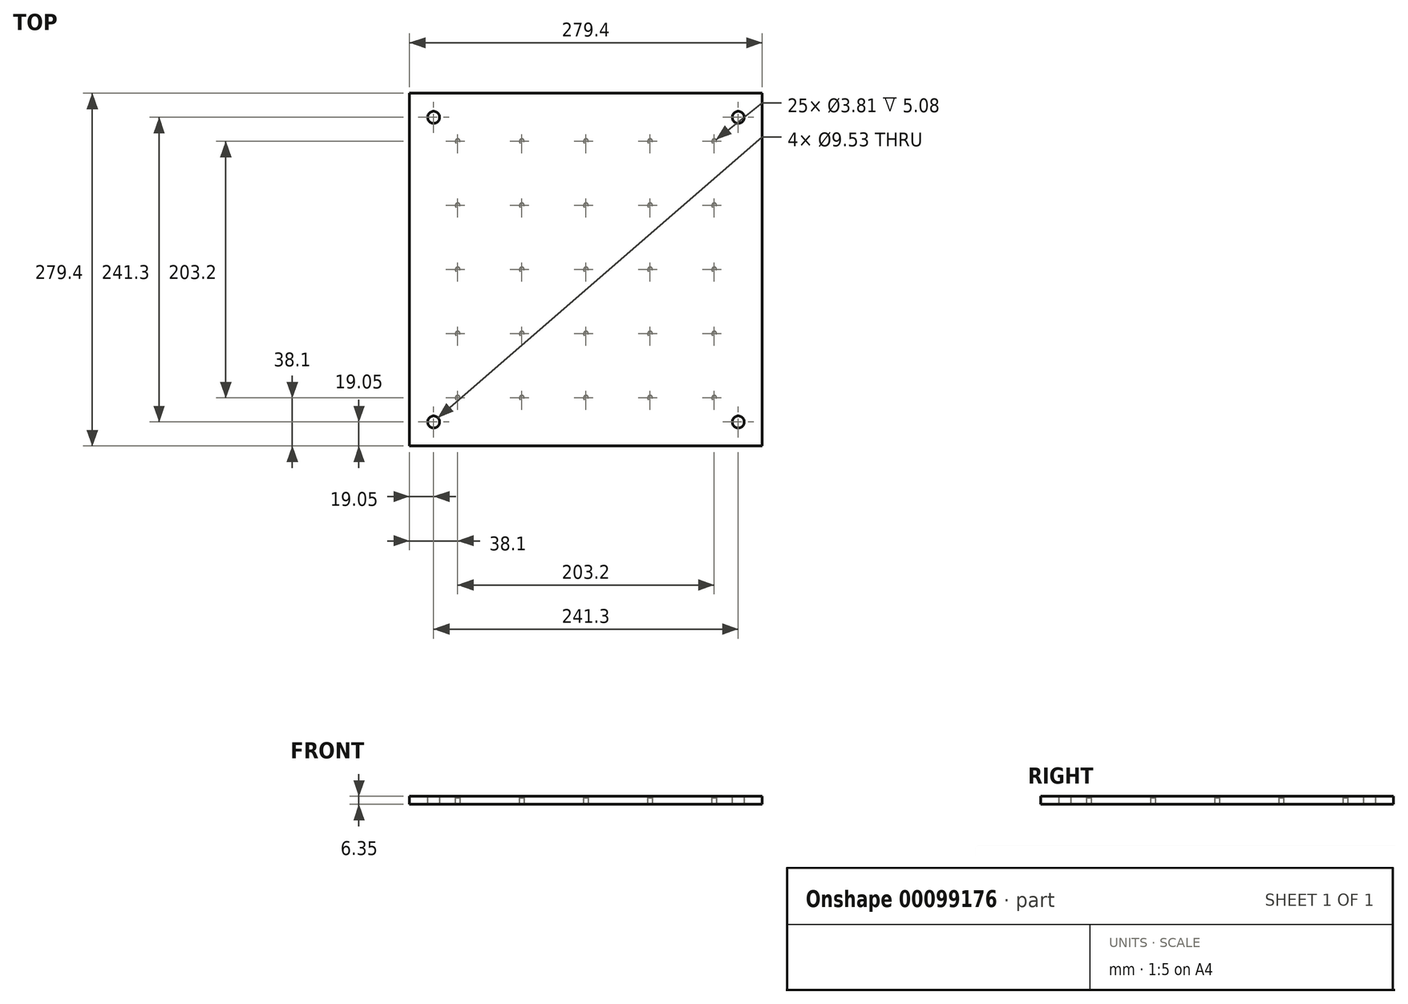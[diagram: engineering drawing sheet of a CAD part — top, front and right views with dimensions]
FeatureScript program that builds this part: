
annotation { "Feature Type Name" : "Feature", "Feature Type Description" : "" }
export const myFeature = defineFeature(function(context is Context, id is Id, definition is map)
    precondition{}
    {
        {
            var Q0;
            Q0=qCreatedBy(makeId("Top.planeOp"),FACE);
            var sketch = newSketch(context, id + "F0", { "sketchPlane" : qUnion([Q0])});
            skLineSegment(sketch, "E0.bottom", {"start": v(0, 0) * mm, "end": v(279.4, 0) * mm});
            skLineSegment(sketch, "E0.top", {"start": v(0, 279.4) * mm, "end": v(279.4, 279.4) * mm});
            skLineSegment(sketch, "E0.left", {"start": v(0, 0) * mm, "end": v(0, 279.4) * mm});
            skLineSegment(sketch, "E0.right", {"start": v(279.4, 0) * mm, "end": v(279.4, 279.4) * mm});
            skSolve(sketch);
        }
        {
            var Q0;
            Q0=makeQuery(id+"F0.imprint","IMPRINT",FACE,{"disambiguationData":[TD([[makeQuery(id+"F0.imprint","IMPRINT",EDGE,{"derivedFrom":sQuery(id+"F0.wireOp",EDGE,"E0.bottom")}),1.0]])]});
            extrude(context, id + "F1", {"entities" : qUnion([Q0]), "depth" : 6.35 * mm});
        }
        {
            var Q0;
            Q0=makeQuery(id+"F1.opExtrude","CAP_FACE",FACE,{"disambiguationData":[OSD([sQuery(id+"F0.wireOp",EDGE,"E0.bottom"),sQuery(id+"F0.wireOp",EDGE,"E0.top"),sQuery(id+"F0.wireOp",EDGE,"E0.left"),sQuery(id+"F0.wireOp",EDGE,"E0.right")])],"isStart":true});
            var sketch = newSketch(context, id + "F2", { "sketchPlane" : qUnion([Q0])});
            skLineSegment(sketch, "E1", {"start": v(0, 0) * mm, "end": v(38.1, 0) * mm, "construction": true});
            skLineSegment(sketch, "E2", {"start": v(38.1, 0) * mm, "end": v(38.1, -38.1) * mm, "construction": true});
            skCircle(sketch, "E3", {"center": v(38.1, -38.1) * mm, "radius": 22.23 * mm, "construction": true});
            skCircle(sketch, "E4.1.0.0", {"center": v(88.9, -38.1) * mm, "radius": 22.23 * mm, "construction": true});
            skCircle(sketch, "E4.2.0.0", {"center": v(139.7, -38.1) * mm, "radius": 22.23 * mm, "construction": true});
            skCircle(sketch, "E4.3.0.0", {"center": v(190.5, -38.1) * mm, "radius": 22.23 * mm, "construction": true});
            skCircle(sketch, "E4.4.0.0", {"center": v(241.3, -38.1) * mm, "radius": 22.23 * mm, "construction": true});
            skLineSegment(sketch, "E4.direction1", {"start": v(38.1, -38.1) * mm, "end": v(88.9, -38.1) * mm, "construction": true});
            skCircle(sketch, "E5.1.0.0", {"center": v(38.1, -88.9) * mm, "radius": 22.23 * mm, "construction": true});
            skCircle(sketch, "E5.1.0.1", {"center": v(88.9, -88.9) * mm, "radius": 22.23 * mm, "construction": true});
            skCircle(sketch, "E5.1.0.2", {"center": v(139.7, -88.9) * mm, "radius": 22.23 * mm, "construction": true});
            skCircle(sketch, "E5.1.0.3", {"center": v(190.5, -88.9) * mm, "radius": 22.23 * mm, "construction": true});
            skCircle(sketch, "E5.1.0.4", {"center": v(241.3, -88.9) * mm, "radius": 22.23 * mm, "construction": true});
            skCircle(sketch, "E5.2.0.0", {"center": v(38.1, -139.7) * mm, "radius": 22.23 * mm, "construction": true});
            skCircle(sketch, "E5.2.0.1", {"center": v(88.9, -139.7) * mm, "radius": 22.23 * mm, "construction": true});
            skCircle(sketch, "E5.2.0.2", {"center": v(139.7, -139.7) * mm, "radius": 22.23 * mm, "construction": true});
            skCircle(sketch, "E5.2.0.3", {"center": v(190.5, -139.7) * mm, "radius": 22.23 * mm, "construction": true});
            skCircle(sketch, "E5.2.0.4", {"center": v(241.3, -139.7) * mm, "radius": 22.23 * mm, "construction": true});
            skCircle(sketch, "E5.3.0.0", {"center": v(38.1, -190.5) * mm, "radius": 22.23 * mm, "construction": true});
            skCircle(sketch, "E5.3.0.1", {"center": v(88.9, -190.5) * mm, "radius": 22.23 * mm, "construction": true});
            skCircle(sketch, "E5.3.0.2", {"center": v(139.7, -190.5) * mm, "radius": 22.23 * mm, "construction": true});
            skCircle(sketch, "E5.3.0.3", {"center": v(190.5, -190.5) * mm, "radius": 22.23 * mm, "construction": true});
            skCircle(sketch, "E5.3.0.4", {"center": v(241.3, -190.5) * mm, "radius": 22.23 * mm, "construction": true});
            skCircle(sketch, "E5.4.0.0", {"center": v(38.1, -241.3) * mm, "radius": 22.23 * mm, "construction": true});
            skCircle(sketch, "E5.4.0.1", {"center": v(88.9, -241.3) * mm, "radius": 22.23 * mm, "construction": true});
            skCircle(sketch, "E5.4.0.2", {"center": v(139.7, -241.3) * mm, "radius": 22.23 * mm, "construction": true});
            skCircle(sketch, "E5.4.0.3", {"center": v(190.5, -241.3) * mm, "radius": 22.23 * mm, "construction": true});
            skCircle(sketch, "E5.4.0.4", {"center": v(241.3, -241.3) * mm, "radius": 22.23 * mm, "construction": true});
            skLineSegment(sketch, "E5.direction1", {"start": v(38.1, -38.1) * mm, "end": v(38.1, -88.9) * mm, "construction": true});
            skCircle(sketch, "E6", {"center": v(38.1, -38.1) * mm, "radius": 1.9 * mm});
            skCircle(sketch, "E7.0.1.0", {"center": v(38.1, -88.9) * mm, "radius": 1.9 * mm});
            skCircle(sketch, "E7.0.2.0", {"center": v(38.1, -139.7) * mm, "radius": 1.9 * mm});
            skCircle(sketch, "E7.0.3.0", {"center": v(38.1, -190.5) * mm, "radius": 1.9 * mm});
            skCircle(sketch, "E7.0.4.0", {"center": v(38.1, -241.3) * mm, "radius": 1.9 * mm});
            skCircle(sketch, "E7.1.0.0", {"center": v(88.9, -38.1) * mm, "radius": 1.9 * mm});
            skCircle(sketch, "E7.1.1.0", {"center": v(88.9, -88.9) * mm, "radius": 1.9 * mm});
            skCircle(sketch, "E7.1.2.0", {"center": v(88.9, -139.7) * mm, "radius": 1.9 * mm});
            skCircle(sketch, "E7.1.3.0", {"center": v(88.9, -190.5) * mm, "radius": 1.9 * mm});
            skCircle(sketch, "E7.1.4.0", {"center": v(88.9, -241.3) * mm, "radius": 1.9 * mm});
            skCircle(sketch, "E7.2.0.0", {"center": v(139.7, -38.1) * mm, "radius": 1.9 * mm});
            skCircle(sketch, "E7.2.1.0", {"center": v(139.7, -88.9) * mm, "radius": 1.9 * mm});
            skCircle(sketch, "E7.2.2.0", {"center": v(139.7, -139.7) * mm, "radius": 1.9 * mm});
            skCircle(sketch, "E7.2.3.0", {"center": v(139.7, -190.5) * mm, "radius": 1.9 * mm});
            skCircle(sketch, "E7.2.4.0", {"center": v(139.7, -241.3) * mm, "radius": 1.9 * mm});
            skCircle(sketch, "E7.3.0.0", {"center": v(190.5, -38.1) * mm, "radius": 1.9 * mm});
            skCircle(sketch, "E7.3.1.0", {"center": v(190.5, -88.9) * mm, "radius": 1.9 * mm});
            skCircle(sketch, "E7.3.2.0", {"center": v(190.5, -139.7) * mm, "radius": 1.9 * mm});
            skCircle(sketch, "E7.3.3.0", {"center": v(190.5, -190.5) * mm, "radius": 1.9 * mm});
            skCircle(sketch, "E7.3.4.0", {"center": v(190.5, -241.3) * mm, "radius": 1.9 * mm});
            skCircle(sketch, "E7.4.0.0", {"center": v(241.3, -38.1) * mm, "radius": 1.9 * mm});
            skCircle(sketch, "E7.4.1.0", {"center": v(241.3, -88.9) * mm, "radius": 1.9 * mm});
            skCircle(sketch, "E7.4.2.0", {"center": v(241.3, -139.7) * mm, "radius": 1.9 * mm});
            skCircle(sketch, "E7.4.3.0", {"center": v(241.3, -190.5) * mm, "radius": 1.9 * mm});
            skCircle(sketch, "E7.4.4.0", {"center": v(241.3, -241.3) * mm, "radius": 1.9 * mm});
            skSolve(sketch);
        }
        {
            var Q0;
            Q0=makeQuery(id+"F2.imprint","IMPRINT",FACE,{"disambiguationData":[TD([[makeQuery(id+"F2.imprint","IMPRINT",EDGE,{"derivedFrom":sQuery(id+"F2.wireOp",EDGE,"E6")}),1.0]])]});
            var Q1;
            Q1=makeQuery(id+"F2.imprint","IMPRINT",FACE,{"disambiguationData":[TD([[makeQuery(id+"F2.imprint","IMPRINT",EDGE,{"derivedFrom":sQuery(id+"F2.wireOp",EDGE,"E7.1.0.0")}),1.0]])]});
            var Q2;
            Q2=makeQuery(id+"F2.imprint","IMPRINT",FACE,{"disambiguationData":[TD([[makeQuery(id+"F2.imprint","IMPRINT",EDGE,{"derivedFrom":sQuery(id+"F2.wireOp",EDGE,"E7.2.0.0")}),1.0]])]});
            var Q3;
            Q3=makeQuery(id+"F2.imprint","IMPRINT",FACE,{"disambiguationData":[TD([[makeQuery(id+"F2.imprint","IMPRINT",EDGE,{"derivedFrom":sQuery(id+"F2.wireOp",EDGE,"E7.4.0.0")}),1.0]])]});
            var Q4;
            Q4=makeQuery(id+"F2.imprint","IMPRINT",FACE,{"disambiguationData":[TD([[makeQuery(id+"F2.imprint","IMPRINT",EDGE,{"derivedFrom":sQuery(id+"F2.wireOp",EDGE,"E7.3.0.0")}),1.0]])]});
            var Q5;
            Q5=makeQuery(id+"F2.imprint","IMPRINT",FACE,{"disambiguationData":[TD([[makeQuery(id+"F2.imprint","IMPRINT",EDGE,{"derivedFrom":sQuery(id+"F2.wireOp",EDGE,"E7.0.1.0")}),1.0]])]});
            var Q6;
            Q6=makeQuery(id+"F2.imprint","IMPRINT",FACE,{"disambiguationData":[TD([[makeQuery(id+"F2.imprint","IMPRINT",EDGE,{"derivedFrom":sQuery(id+"F2.wireOp",EDGE,"E7.1.1.0")}),1.0]])]});
            var Q7;
            Q7=makeQuery(id+"F2.imprint","IMPRINT",FACE,{"disambiguationData":[TD([[makeQuery(id+"F2.imprint","IMPRINT",EDGE,{"derivedFrom":sQuery(id+"F2.wireOp",EDGE,"E7.2.1.0")}),1.0]])]});
            var Q8;
            Q8=makeQuery(id+"F2.imprint","IMPRINT",FACE,{"disambiguationData":[TD([[makeQuery(id+"F2.imprint","IMPRINT",EDGE,{"derivedFrom":sQuery(id+"F2.wireOp",EDGE,"E7.3.1.0")}),1.0]])]});
            var Q9;
            Q9=makeQuery(id+"F2.imprint","IMPRINT",FACE,{"disambiguationData":[TD([[makeQuery(id+"F2.imprint","IMPRINT",EDGE,{"derivedFrom":sQuery(id+"F2.wireOp",EDGE,"E7.4.1.0")}),1.0]])]});
            var Q10;
            Q10=makeQuery(id+"F2.imprint","IMPRINT",FACE,{"disambiguationData":[TD([[makeQuery(id+"F2.imprint","IMPRINT",EDGE,{"derivedFrom":sQuery(id+"F2.wireOp",EDGE,"E7.0.2.0")}),1.0]])]});
            var Q11;
            Q11=makeQuery(id+"F2.imprint","IMPRINT",FACE,{"disambiguationData":[TD([[makeQuery(id+"F2.imprint","IMPRINT",EDGE,{"derivedFrom":sQuery(id+"F2.wireOp",EDGE,"E7.1.2.0")}),1.0]])]});
            var Q12;
            Q12=makeQuery(id+"F2.imprint","IMPRINT",FACE,{"disambiguationData":[TD([[makeQuery(id+"F2.imprint","IMPRINT",EDGE,{"derivedFrom":sQuery(id+"F2.wireOp",EDGE,"E7.2.2.0")}),1.0]])]});
            var Q13;
            Q13=makeQuery(id+"F2.imprint","IMPRINT",FACE,{"disambiguationData":[TD([[makeQuery(id+"F2.imprint","IMPRINT",EDGE,{"derivedFrom":sQuery(id+"F2.wireOp",EDGE,"E7.3.2.0")}),1.0]])]});
            var Q14;
            Q14=makeQuery(id+"F2.imprint","IMPRINT",FACE,{"disambiguationData":[TD([[makeQuery(id+"F2.imprint","IMPRINT",EDGE,{"derivedFrom":sQuery(id+"F2.wireOp",EDGE,"E7.4.2.0")}),1.0]])]});
            var Q15;
            Q15=makeQuery(id+"F2.imprint","IMPRINT",FACE,{"disambiguationData":[TD([[makeQuery(id+"F2.imprint","IMPRINT",EDGE,{"derivedFrom":sQuery(id+"F2.wireOp",EDGE,"E7.4.3.0")}),1.0]])]});
            var Q16;
            Q16=makeQuery(id+"F2.imprint","IMPRINT",FACE,{"disambiguationData":[TD([[makeQuery(id+"F2.imprint","IMPRINT",EDGE,{"derivedFrom":sQuery(id+"F2.wireOp",EDGE,"E7.3.3.0")}),1.0]])]});
            var Q17;
            Q17=makeQuery(id+"F2.imprint","IMPRINT",FACE,{"disambiguationData":[TD([[makeQuery(id+"F2.imprint","IMPRINT",EDGE,{"derivedFrom":sQuery(id+"F2.wireOp",EDGE,"E7.2.3.0")}),1.0]])]});
            var Q18;
            Q18=makeQuery(id+"F2.imprint","IMPRINT",FACE,{"disambiguationData":[TD([[makeQuery(id+"F2.imprint","IMPRINT",EDGE,{"derivedFrom":sQuery(id+"F2.wireOp",EDGE,"E7.1.3.0")}),1.0]])]});
            var Q19;
            Q19=makeQuery(id+"F2.imprint","IMPRINT",FACE,{"disambiguationData":[TD([[makeQuery(id+"F2.imprint","IMPRINT",EDGE,{"derivedFrom":sQuery(id+"F2.wireOp",EDGE,"E7.0.3.0")}),1.0]])]});
            var Q20;
            Q20=makeQuery(id+"F2.imprint","IMPRINT",FACE,{"disambiguationData":[TD([[makeQuery(id+"F2.imprint","IMPRINT",EDGE,{"derivedFrom":sQuery(id+"F2.wireOp",EDGE,"E7.0.4.0")}),1.0]])]});
            var Q21;
            Q21=makeQuery(id+"F2.imprint","IMPRINT",FACE,{"disambiguationData":[TD([[makeQuery(id+"F2.imprint","IMPRINT",EDGE,{"derivedFrom":sQuery(id+"F2.wireOp",EDGE,"E7.1.4.0")}),1.0]])]});
            var Q22;
            Q22=makeQuery(id+"F2.imprint","IMPRINT",FACE,{"disambiguationData":[TD([[makeQuery(id+"F2.imprint","IMPRINT",EDGE,{"derivedFrom":sQuery(id+"F2.wireOp",EDGE,"E7.2.4.0")}),1.0]])]});
            var Q23;
            Q23=makeQuery(id+"F2.imprint","IMPRINT",FACE,{"disambiguationData":[TD([[makeQuery(id+"F2.imprint","IMPRINT",EDGE,{"derivedFrom":sQuery(id+"F2.wireOp",EDGE,"E7.3.4.0")}),1.0]])]});
            var Q24;
            Q24=makeQuery(id+"F2.imprint","IMPRINT",FACE,{"disambiguationData":[TD([[makeQuery(id+"F2.imprint","IMPRINT",EDGE,{"derivedFrom":sQuery(id+"F2.wireOp",EDGE,"E7.4.4.0")}),1.0]])]});
            extrude(context, id + "F3", {"entities" : qUnion([Q0, Q1, Q2, Q3, Q4, Q5, Q6, Q7, Q8, Q9, Q10, Q11, Q12, Q13, Q14, Q15, Q16, Q17, Q18, Q19, Q20, Q21, Q22, Q23, Q24]), "operationType" : NewBodyOperationType.REMOVE, "oppositeDirection" : true, "depth" : 5.08 * mm});
        }
        {
            var Q0;
            Q0=makeQuery(id+"F1.opExtrude","CAP_FACE",FACE,{"disambiguationData":[OSD([sQuery(id+"F0.wireOp",EDGE,"E0.bottom"),sQuery(id+"F0.wireOp",EDGE,"E0.top"),sQuery(id+"F0.wireOp",EDGE,"E0.left"),sQuery(id+"F0.wireOp",EDGE,"E0.right")])],"isStart":true});
            var sketch = newSketch(context, id + "F4", { "sketchPlane" : qUnion([Q0])});
            skLineSegment(sketch, "E8", {"start": v(0, 0) * mm, "end": v(38.1, -38.1) * mm, "construction": true});
            skLineSegment(sketch, "E9", {"start": v(38.1, -38.1) * mm, "end": v(19.05, -19.05) * mm, "construction": true});
            skCircle(sketch, "E10", {"center": v(19.05, -19.05) * mm, "radius": 4.76 * mm});
            skCircle(sketch, "E11.0.1.0", {"center": v(19.05, -260.35) * mm, "radius": 4.76 * mm});
            skCircle(sketch, "E11.1.0.0", {"center": v(260.35, -19.05) * mm, "radius": 4.76 * mm});
            skCircle(sketch, "E11.1.1.0", {"center": v(260.35, -260.35) * mm, "radius": 4.76 * mm});
            skLineSegment(sketch, "E11.direction1", {"start": v(19.05, -19.05) * mm, "end": v(260.35, -19.05) * mm, "construction": true});
            skLineSegment(sketch, "E11.direction2", {"start": v(19.05, -19.05) * mm, "end": v(19.05, -260.35) * mm, "construction": true});
            skSolve(sketch);
        }
        {
            var Q0;
            Q0=makeQuery(id+"F4.imprint","IMPRINT",FACE,{"disambiguationData":[TD([[makeQuery(id+"F4.imprint","IMPRINT",EDGE,{"derivedFrom":sQuery(id+"F4.wireOp",EDGE,"E10")}),1.0]])]});
            var Q1;
            Q1=makeQuery(id+"F4.imprint","IMPRINT",FACE,{"disambiguationData":[TD([[makeQuery(id+"F4.imprint","IMPRINT",EDGE,{"derivedFrom":sQuery(id+"F4.wireOp",EDGE,"E11.1.1.0")}),1.0]])]});
            var Q2;
            Q2=makeQuery(id+"F4.imprint","IMPRINT",FACE,{"disambiguationData":[TD([[makeQuery(id+"F4.imprint","IMPRINT",EDGE,{"derivedFrom":sQuery(id+"F4.wireOp",EDGE,"E11.0.1.0")}),1.0]])]});
            var Q3;
            Q3=makeQuery(id+"F4.imprint","IMPRINT",FACE,{"disambiguationData":[TD([[makeQuery(id+"F4.imprint","IMPRINT",EDGE,{"derivedFrom":sQuery(id+"F4.wireOp",EDGE,"E11.1.0.0")}),1.0]])]});
            extrude(context, id + "F5", {"entities" : qUnion([Q0, Q1, Q2, Q3]), "operationType" : NewBodyOperationType.REMOVE, "endBound" : BoundingType.THROUGH_ALL, "oppositeDirection" : true, "depth" : 25.4 * mm});
        }
    });
